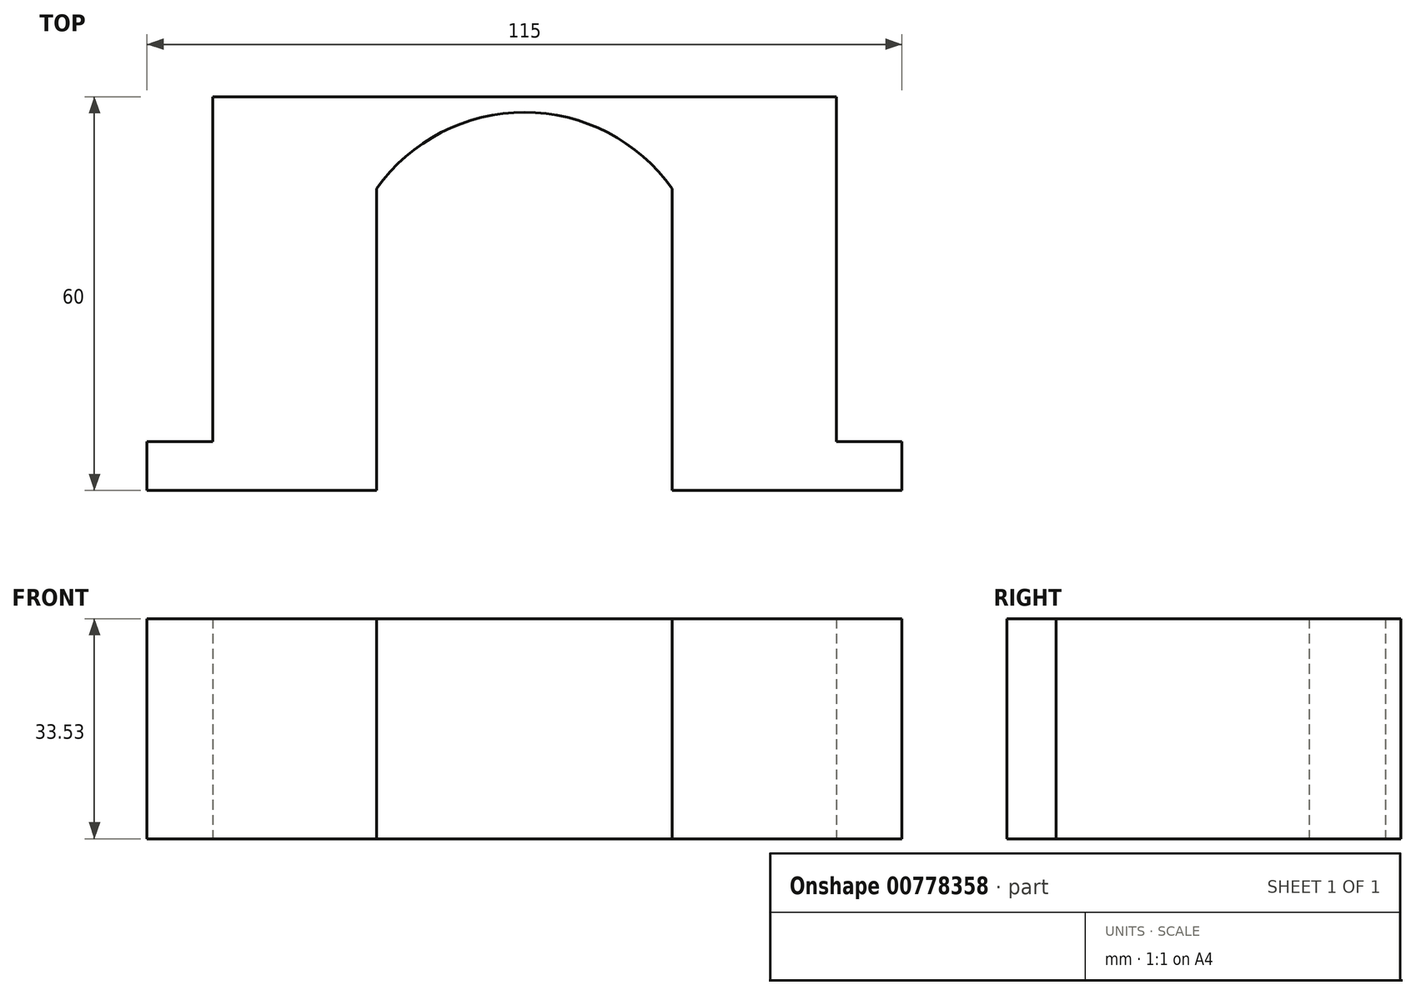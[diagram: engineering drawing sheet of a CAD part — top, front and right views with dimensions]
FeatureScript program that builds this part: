
annotation { "Feature Type Name" : "Feature", "Feature Type Description" : "" }
export const myFeature = defineFeature(function(context is Context, id is Id, definition is map)
    precondition{}
    {
        {
            var Q0;
            Q0=qCreatedBy(makeId("Top.planeOp"),FACE);
            var sketch = newSketch(context, id + "F0", { "sketchPlane" : qUnion([Q0])});
            skLineSegment(sketch, "E0.bottom", {"start": v(-47.5, 30) * mm, "end": v(47.5, 30) * mm});
            skLineSegment(sketch, "E0.top", {"start": v(-47.5, -30) * mm, "end": v(47.5, -30) * mm});
            skLineSegment(sketch, "E0.left", {"start": v(-47.5, 30) * mm, "end": v(-47.5, -22.52) * mm});
            skLineSegment(sketch, "E0.right", {"start": v(47.5, 30) * mm, "end": v(47.5, -22.52) * mm});
            skPoint(sketch, "E0.middle", {"position": v(0, 0) * mm});
            skLineSegment(sketch, "E1.top", {"start": v(0, -30) * mm, "end": v(-57.5, -30) * mm});
            skLineSegment(sketch, "E1.left", {"start": v(0, -27.62) * mm, "end": v(0, -30) * mm});
            skLineSegment(sketch, "E1.right", {"start": v(-57.5, -22.52) * mm, "end": v(-57.5, -30) * mm});
            skLineSegment(sketch, "E2", {"start": v(-22.5, 16.02) * mm, "end": v(-22.5, 0) * mm});
            skArc(sketch, "E3", {"start": v(22.5, 16.02) * mm, "mid": v(0, 27.62) * mm, "end": v(-22.5, 16.02) * mm});
            skLineSegment(sketch, "E4.trimOffspring", {"start": v(-47.5, -22.52) * mm, "end": v(-57.5, -22.52) * mm});
            skLineSegment(sketch, "E5", {"start": v(-22.5, 0) * mm, "end": v(-22.5, -30) * mm});
            skLineSegment(sketch, "E6.MirrorCS", {"start": v(57.5, -22.52) * mm, "end": v(57.5, -30) * mm});
            skLineSegment(sketch, "E7.MirrorCS", {"start": v(47.5, -22.52) * mm, "end": v(57.5, -22.52) * mm});
            skLineSegment(sketch, "E8.MirrorCS", {"start": v(47.5, 30) * mm, "end": v(-47.5, 30) * mm});
            skLineSegment(sketch, "E9.MirrorCS", {"start": v(22.5, 16.02) * mm, "end": v(22.5, 0) * mm});
            skLineSegment(sketch, "E10.MirrorCS", {"start": v(22.5, 0) * mm, "end": v(22.5, -30) * mm});
            skLineSegment(sketch, "E11.MirrorCS", {"start": v(0, -30) * mm, "end": v(57.5, -30) * mm});
            skArc(sketch, "E12.trimOffspring", {"start": v(-22.5, 16.02) * mm, "mid": v(0, 27.62) * mm, "end": v(22.5, 16.02) * mm});
            skPoint(sketch, "E13.MirrorCS.start.orphan", {"position": v(0, -27.62) * mm});
            skPoint(sketch, "E14.orphan", {"position": v(47.5, -30) * mm});
            skLineSegment(sketch, "E15", {"start": v(-47.5, -22.52) * mm, "end": v(-47.5, -30) * mm});
            skLineSegment(sketch, "E16", {"start": v(47.5, -22.52) * mm, "end": v(47.5, -30) * mm});
            skSolve(sketch);
        }
        {
            var Q0;
            {var subQ0=sQuery(id+"F0.wireOp",EDGE,"E1.right");Q0=makeQuery(id+"F0.imprint","IMPRINT",FACE,{"disambiguationData":[TD([[makeQuery(id+"F0.imprint","IMPRINT",EDGE,{"derivedFrom":subQ0}),1.0]])]});}
            var Q1;
            {var subQ0=sQuery(id+"F0.wireOp",EDGE,"E6.MirrorCS");Q1=makeQuery(id+"F0.imprint","IMPRINT",FACE,{"disambiguationData":[TD([[makeQuery(id+"F0.imprint","IMPRINT",EDGE,{"derivedFrom":subQ0}),-1.0]])]});}
            var Q2;
            {var subQ2=sQuery(id+"F0.wireOp",EDGE,"E0.right");Q2=makeQuery(id+"F0.imprint","IMPRINT",FACE,{"disambiguationData":[TD([[makeQuery(id+"F0.imprint","IMPRINT",EDGE,{"derivedFrom":subQ2}),-1.0]])]});}
            var Q3;
            {var subQ4=sQuery(id+"F0.wireOp",EDGE,"E0.left");Q3=makeQuery(id+"F0.imprint","IMPRINT",FACE,{"disambiguationData":[TD([[makeQuery(id+"F0.imprint","IMPRINT",EDGE,{"derivedFrom":subQ4}),1.0]])]});}
            extrude(context, id + "F1", {"entities" : qUnion([Q0, Q1, Q2, Q3]), "depth" : 33.53 * mm, "offsetDistance" : 25.4 * mm});
        }
    });
